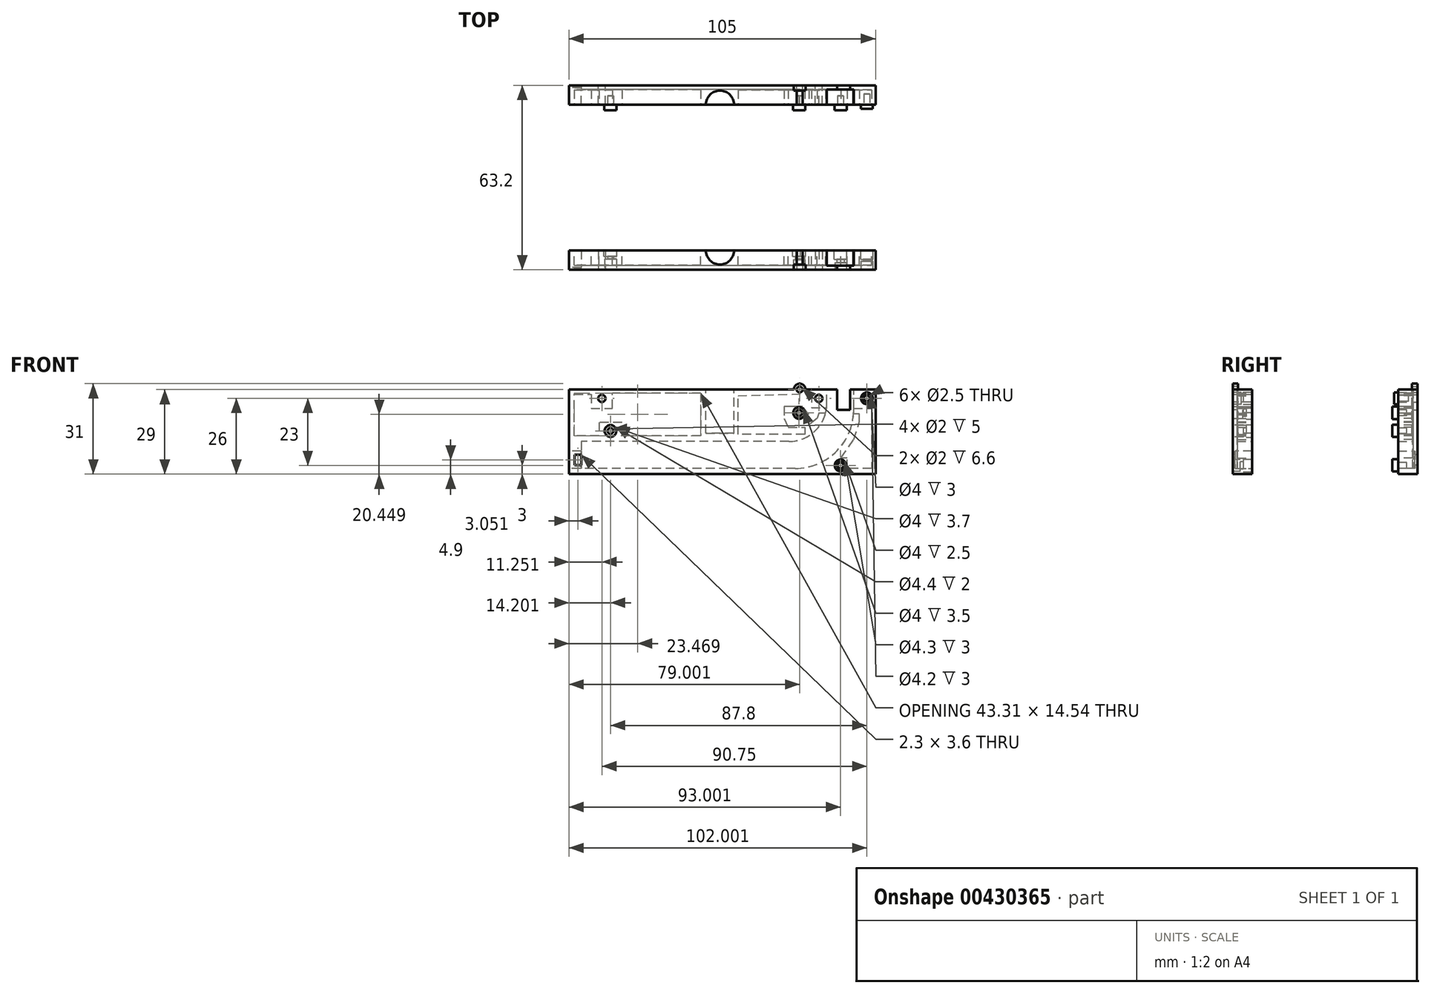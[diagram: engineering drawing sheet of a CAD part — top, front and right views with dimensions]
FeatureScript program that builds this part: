
annotation { "Feature Type Name" : "Feature", "Feature Type Description" : "" }
export const myFeature = defineFeature(function(context is Context, id is Id, definition is map)
    precondition{}
    {
        {
            var Q0;
            Q0=qCreatedBy(makeId("Front.planeOp"),FACE);
            var sketch = newSketch(context, id + "F0", { "sketchPlane" : qUnion([Q0])});
            skLineSegment(sketch, "E0.bottom", {"start": v(-55.53, -4.5) * mm, "end": v(49.47, -4.5) * mm});
            skLineSegment(sketch, "E0.top", {"start": v(-55.53, -33.5) * mm, "end": v(49.47, -33.5) * mm});
            skLineSegment(sketch, "E0.left", {"start": v(-55.53, -4.5) * mm, "end": v(-55.53, -33.5) * mm});
            skLineSegment(sketch, "E0.right", {"start": v(49.47, -4.5) * mm, "end": v(49.47, -33.5) * mm});
            skSolve(sketch);
        }
        {
            var Q0;
            Q0 = qSketchRegion(id + "F0", true);
            extrude(context, id + "F1", {"entities" : qUnion([Q0]), "depth" : 6.6 * mm});
        }
        {
            var Q0;
            Q0=makeQuery(id+"F1.opExtrude","CAP_FACE",FACE,{"disambiguationData":[OSD([sQuery(id+"F0.wireOp",EDGE,"E0.bottom"),sQuery(id+"F0.wireOp",EDGE,"E0.top"),sQuery(id+"F0.wireOp",EDGE,"E0.left"),sQuery(id+"F0.wireOp",EDGE,"E0.right")])],"isStart":false});
            var sketch = newSketch(context, id + "F2", { "sketchPlane" : qUnion([Q0])});
            skCircle(sketch, "E1", {"center": v(46.47, -7.5) * mm, "radius": 2 * mm});
            skSolve(sketch);
        }
        {
            var Q0;
            Q0 = qSketchRegion(id + "F2", true);
            extrude(context, id + "F3", {"entities" : qUnion([Q0]), "operationType" : NewBodyOperationType.REMOVE, "oppositeDirection" : true, "depth" : 3 * mm});
        }
        {
            var Q0;
            Q0=makeQuery(id+"F3.boolean.opBoolean","COPY",FACE,{"derivedFrom":makeQuery(id+"F3.opExtrude","CAP_FACE",FACE,{"disambiguationData":[OSD([sQuery(id+"F2.wireOp",EDGE,"E1")])],"isStart":false})});
            var sketch = newSketch(context, id + "F4", { "sketchPlane" : qUnion([Q0])});
            skCircle(sketch, "E2", {"center": v(46.47, -7.5) * mm, "radius": 1.25 * mm});
            skSolve(sketch);
        }
        {
            var Q0;
            Q0 = qSketchRegion(id + "F4", true);
            extrude(context, id + "F5", {"entities" : qUnion([Q0]), "operationType" : NewBodyOperationType.REMOVE, "oppositeDirection" : true, "depth" : 25 * mm});
        }
        {
            var Q0;
            Q0=makeQuery(id+"F1.opExtrude","CAP_FACE",FACE,{"disambiguationData":[OSD([sQuery(id+"F0.wireOp",EDGE,"E0.bottom"),sQuery(id+"F0.wireOp",EDGE,"E0.top"),sQuery(id+"F0.wireOp",EDGE,"E0.left"),sQuery(id+"F0.wireOp",EDGE,"E0.right")])],"isStart":false});
            var sketch = newSketch(context, id + "F6", { "sketchPlane" : qUnion([Q0])});
            skCircle(sketch, "E3", {"center": v(30.02, -7.55) * mm, "radius": 1.25 * mm});
            skSolve(sketch);
        }
        {
            var Q0;
            Q0 = qSketchRegion(id + "F6", true);
            extrude(context, id + "F7", {"entities" : qUnion([Q0]), "operationType" : NewBodyOperationType.REMOVE, "oppositeDirection" : true, "depth" : 25 * mm});
        }
        {
            var Q0;
            Q0=makeQuery(id+"F1.opExtrude","CAP_FACE",FACE,{"disambiguationData":[OSD([sQuery(id+"F0.wireOp",EDGE,"E0.bottom"),sQuery(id+"F0.wireOp",EDGE,"E0.top"),sQuery(id+"F0.wireOp",EDGE,"E0.left"),sQuery(id+"F0.wireOp",EDGE,"E0.right")])],"isStart":false});
            var sketch = newSketch(context, id + "F8", { "sketchPlane" : qUnion([Q0])});
            skCircle(sketch, "E4", {"center": v(23.27, -12.5) * mm, "radius": 1 * mm});
            skSolve(sketch);
        }
        {
            var Q0;
            Q0 = qSketchRegion(id + "F8", true);
            extrude(context, id + "F9", {"entities" : qUnion([Q0]), "operationType" : NewBodyOperationType.REMOVE, "oppositeDirection" : true, "depth" : 3.7 * mm});
        }
        {
            var Q0;
            Q0=makeQuery(id+"F9.boolean.opBoolean","COPY",FACE,{"derivedFrom":makeQuery(id+"F9.opExtrude","CAP_FACE",FACE,{"disambiguationData":[OSD([sQuery(id+"F8.wireOp",EDGE,"E4")])],"isStart":false})});
            var sketch = newSketch(context, id + "F10", { "sketchPlane" : qUnion([Q0])});
            skCircle(sketch, "E5", {"center": v(23.27, -12.5) * mm, "radius": 1.3 * mm});
            skSolve(sketch);
        }
        {
            var Q0;
            Q0 = qSketchRegion(id + "F10", true);
            extrude(context, id + "F11", {"entities" : qUnion([Q0]), "operationType" : NewBodyOperationType.REMOVE, "oppositeDirection" : true, "depth" : 25 * mm});
        }
        {
            var Q0;
            Q0=makeQuery(id+"F1.opExtrude","CAP_FACE",FACE,{"disambiguationData":[OSD([sQuery(id+"F0.wireOp",EDGE,"E0.bottom"),sQuery(id+"F0.wireOp",EDGE,"E0.top"),sQuery(id+"F0.wireOp",EDGE,"E0.left"),sQuery(id+"F0.wireOp",EDGE,"E0.right")])],"isStart":false});
            var sketch = newSketch(context, id + "F12", { "sketchPlane" : qUnion([Q0])});
            skCircle(sketch, "E6", {"center": v(-44.28, -7.55) * mm, "radius": 1.25 * mm});
            skSolve(sketch);
        }
        {
            var Q0;
            Q0 = qSketchRegion(id + "F12", true);
            extrude(context, id + "F13", {"entities" : qUnion([Q0]), "operationType" : NewBodyOperationType.REMOVE, "oppositeDirection" : true, "depth" : 25 * mm});
        }
        {
            var Q0;
            Q0=makeQuery(id+"F1.opExtrude","CAP_FACE",FACE,{"disambiguationData":[OSD([sQuery(id+"F0.wireOp",EDGE,"E0.bottom"),sQuery(id+"F0.wireOp",EDGE,"E0.top"),sQuery(id+"F0.wireOp",EDGE,"E0.left"),sQuery(id+"F0.wireOp",EDGE,"E0.right")])],"isStart":false});
            var sketch = newSketch(context, id + "F14", { "sketchPlane" : qUnion([Q0])});
            skCircle(sketch, "E7", {"center": v(-41.33, -18.7) * mm, "radius": 2 * mm});
            skSolve(sketch);
        }
        {
            var Q0;
            Q0 = qSketchRegion(id + "F14", true);
            extrude(context, id + "F15", {"entities" : qUnion([Q0]), "operationType" : NewBodyOperationType.REMOVE, "oppositeDirection" : true, "depth" : 3.7 * mm});
        }
        {
            var Q0;
            Q0=makeQuery(id+"F15.boolean.opBoolean","COPY",FACE,{"derivedFrom":makeQuery(id+"F15.opExtrude","CAP_FACE",FACE,{"disambiguationData":[OSD([sQuery(id+"F14.wireOp",EDGE,"E7")])],"isStart":false})});
            var sketch = newSketch(context, id + "F16", { "sketchPlane" : qUnion([Q0])});
            skCircle(sketch, "E8", {"center": v(-41.33, -18.7) * mm, "radius": 1 * mm});
            skSolve(sketch);
        }
        {
            var Q0;
            Q0 = qSketchRegion(id + "F16", true);
            extrude(context, id + "F17", {"entities" : qUnion([Q0]), "operationType" : NewBodyOperationType.REMOVE, "oppositeDirection" : true, "depth" : 25 * mm});
        }
        {
            var Q0;
            Q0=makeQuery(id+"F1.opExtrude","CAP_FACE",FACE,{"disambiguationData":[OSD([sQuery(id+"F0.wireOp",EDGE,"E0.bottom"),sQuery(id+"F0.wireOp",EDGE,"E0.top"),sQuery(id+"F0.wireOp",EDGE,"E0.left"),sQuery(id+"F0.wireOp",EDGE,"E0.right")])],"isStart":false});
            var sketch = newSketch(context, id + "F18", { "sketchPlane" : qUnion([Q0])});
            skCircle(sketch, "E9", {"center": v(37.47, -30.5) * mm, "radius": 2 * mm});
            skSolve(sketch);
        }
        {
            var Q0;
            Q0 = qSketchRegion(id + "F18", true);
            extrude(context, id + "F19", {"entities" : qUnion([Q0]), "operationType" : NewBodyOperationType.REMOVE, "oppositeDirection" : true, "depth" : 2.5 * mm});
        }
        {
            var Q0;
            Q0=makeQuery(id+"F19.boolean.opBoolean","COPY",FACE,{"derivedFrom":makeQuery(id+"F19.opExtrude","CAP_FACE",FACE,{"disambiguationData":[OSD([sQuery(id+"F18.wireOp",EDGE,"E9")])],"isStart":false})});
            var sketch = newSketch(context, id + "F20", { "sketchPlane" : qUnion([Q0])});
            skCircle(sketch, "E10", {"center": v(37.47, -30.5) * mm, "radius": 1.25 * mm});
            skSolve(sketch);
        }
        {
            var Q0;
            Q0 = qSketchRegion(id + "F20", true);
            extrude(context, id + "F21", {"entities" : qUnion([Q0]), "operationType" : NewBodyOperationType.REMOVE, "oppositeDirection" : true, "depth" : 25 * mm});
        }
        {
            var Q0;
            Q0=makeQuery(id+"F1.opExtrude","CAP_FACE",FACE,{"disambiguationData":[OSD([sQuery(id+"F0.wireOp",EDGE,"E0.bottom"),sQuery(id+"F0.wireOp",EDGE,"E0.top"),sQuery(id+"F0.wireOp",EDGE,"E0.left"),sQuery(id+"F0.wireOp",EDGE,"E0.right")])],"isStart":false});
            var sketch = newSketch(context, id + "F22", { "sketchPlane" : qUnion([Q0])});
            skLineSegment(sketch, "E11.bottom", {"start": v(36.27, -4.5) * mm, "end": v(40.77, -4.5) * mm});
            skLineSegment(sketch, "E11.top", {"start": v(36.27, -11.5) * mm, "end": v(40.77, -11.5) * mm});
            skLineSegment(sketch, "E11.left", {"start": v(36.27, -4.5) * mm, "end": v(36.27, -11.5) * mm});
            skLineSegment(sketch, "E11.right", {"start": v(40.77, -4.5) * mm, "end": v(40.77, -11.5) * mm});
            skSolve(sketch);
        }
        {
            var Q0;
            Q0 = qSketchRegion(id + "F22", true);
            extrude(context, id + "F23", {"entities" : qUnion([Q0]), "operationType" : NewBodyOperationType.REMOVE, "oppositeDirection" : true, "depth" : 25 * mm});
        }
        {
            var Q0;
            Q0=makeQuery(id+"F1.opExtrude","CAP_FACE",FACE,{"disambiguationData":[OSD([sQuery(id+"F0.wireOp",EDGE,"E0.bottom"),sQuery(id+"F0.wireOp",EDGE,"E0.top"),sQuery(id+"F0.wireOp",EDGE,"E0.left"),sQuery(id+"F0.wireOp",EDGE,"E0.right")])],"isStart":false});
            var sketch = newSketch(context, id + "F24", { "sketchPlane" : qUnion([Q0])});
            skCircle(sketch, "E12", {"center": v(23.47, -4.5) * mm, "radius": 2 * mm});
            skSolve(sketch);
        }
        {
            var Q0;
            Q0 = qSketchRegion(id + "F24", true);
            extrude(context, id + "F25", {"entities" : qUnion([Q0]), "operationType" : NewBodyOperationType.ADD, "oppositeDirection" : true, "depth" : 1.8 * mm});
        }
        {
            var Q0;
            Q0=makeQuery(id+"F25.boolean.opBoolean","MERGE",FACE,{"derivedFrom":[makeQuery(id+"F1.opExtrude","CAP_FACE",FACE,{"disambiguationData":[OSD([sQuery(id+"F0.wireOp",EDGE,"E0.bottom"),sQuery(id+"F0.wireOp",EDGE,"E0.top"),sQuery(id+"F0.wireOp",EDGE,"E0.left"),sQuery(id+"F0.wireOp",EDGE,"E0.right")])],"isStart":false}),makeQuery(id+"F25.opExtrude","CAP_FACE",FACE,{"disambiguationData":[OSD([sQuery(id+"F24.wireOp",EDGE,"E12")])],"isStart":true})]});
            var sketch = newSketch(context, id + "F26", { "sketchPlane" : qUnion([Q0])});
            skCircle(sketch, "E13", {"center": v(23.47, -4.5) * mm, "radius": 1 * mm});
            skSolve(sketch);
        }
        {
            var Q0;
            Q0 = qSketchRegion(id + "F26", true);
            extrude(context, id + "F27", {"entities" : qUnion([Q0]), "operationType" : NewBodyOperationType.REMOVE, "oppositeDirection" : true, "depth" : 25 * mm});
        }
        {
            var Q0;
            Q0=makeQuery(id+"F25.boolean.opBoolean","MERGE",FACE,{"derivedFrom":[makeQuery(id+"F1.opExtrude","CAP_FACE",FACE,{"disambiguationData":[OSD([sQuery(id+"F0.wireOp",EDGE,"E0.bottom"),sQuery(id+"F0.wireOp",EDGE,"E0.top"),sQuery(id+"F0.wireOp",EDGE,"E0.left"),sQuery(id+"F0.wireOp",EDGE,"E0.right")])],"isStart":false}),makeQuery(id+"F25.opExtrude","CAP_FACE",FACE,{"disambiguationData":[OSD([sQuery(id+"F24.wireOp",EDGE,"E12")])],"isStart":true})]});
            var sketch = newSketch(context, id + "F28", { "sketchPlane" : qUnion([Q0])});
            skLineSegment(sketch, "E14.bottom", {"start": v(-42.43, -33.5) * mm, "end": v(35.07, -33.5) * mm});
            skLineSegment(sketch, "E14.top", {"start": v(-42.43, -32.1) * mm, "end": v(35.07, -32.1) * mm});
            skLineSegment(sketch, "E14.left", {"start": v(-42.43, -33.5) * mm, "end": v(-42.43, -32.1) * mm});
            skLineSegment(sketch, "E14.right", {"start": v(35.07, -33.5) * mm, "end": v(35.07, -32.1) * mm});
            skSolve(sketch);
        }
        {
            var Q0;
            Q0=makeQuery(id+"F1.opExtrude","CAP_FACE",FACE,{"disambiguationData":[OSD([sQuery(id+"F0.wireOp",EDGE,"E0.bottom"),sQuery(id+"F0.wireOp",EDGE,"E0.top"),sQuery(id+"F0.wireOp",EDGE,"E0.left"),sQuery(id+"F0.wireOp",EDGE,"E0.right")])],"isStart":true});
            var sketch = newSketch(context, id + "F29", { "sketchPlane" : qUnion([Q0])});
            skArc(sketch, "E15", {"start": v(-41.96, -10.9) * mm, "mid": v(-36.32, -25.43) * mm, "end": v(-21.97, -31.5) * mm});
            skLineSegment(sketch, "E16", {"start": v(-41.96, -12.1) * mm, "end": v(-41.96, -4.5) * mm});
            skLineSegment(sketch, "E17", {"start": v(-41.96, -4.5) * mm, "end": v(-40.77, -4.5) * mm});
            skLineSegment(sketch, "E18", {"start": v(-21.97, -31.5) * mm, "end": v(55.53, -31.5) * mm});
            skLineSegment(sketch, "E19", {"start": v(-40.77, -4.5) * mm, "end": v(-40.77, -11.5) * mm});
            skLineSegment(sketch, "E20", {"start": v(-40.77, -11.5) * mm, "end": v(-36.27, -11.5) * mm});
            skLineSegment(sketch, "E21", {"start": v(-36.27, -11.5) * mm, "end": v(-36.27, -4.5) * mm});
            skLineSegment(sketch, "E22", {"start": v(-36.27, -4.5) * mm, "end": v(-32.76, -4.5) * mm});
            skArc(sketch, "E23", {"start": v(-32.76, -9.3) * mm, "mid": v(-28.95, -18.5) * mm, "end": v(-19.76, -22.3) * mm});
            skLineSegment(sketch, "E24", {"start": v(-32.76, -9.3) * mm, "end": v(-32.76, -4.5) * mm});
            skLineSegment(sketch, "E25", {"start": v(-19.76, -22.3) * mm, "end": v(-17.97, -22.3) * mm});
            skLineSegment(sketch, "E26", {"start": v(-17.97, -22.3) * mm, "end": v(55.53, -22.3) * mm});
            skLineSegment(sketch, "E27", {"start": v(55.53, -31.5) * mm, "end": v(55.53, -22.3) * mm});
            skSolve(sketch);
        }
        {
            var Q0;
            Q0 = qSketchRegion(id + "F29", true);
            extrude(context, id + "F30", {"entities" : qUnion([Q0]), "operationType" : NewBodyOperationType.REMOVE, "oppositeDirection" : true, "depth" : 5.1 * mm});
        }
        {
            var Q0;
            Q0=makeQuery(id+"F30.boolean.opBoolean","COPY",FACE,{"derivedFrom":makeQuery(id+"F30.opExtrude","CAP_FACE",FACE,{"disambiguationData":[OSD([sQuery(id+"F29.wireOp",EDGE,"E15"),sQuery(id+"F29.wireOp",EDGE,"E16"),sQuery(id+"F29.wireOp",EDGE,"E17"),sQuery(id+"F29.wireOp",EDGE,"E18"),sQuery(id+"F29.wireOp",EDGE,"E19"),sQuery(id+"F29.wireOp",EDGE,"E20"),sQuery(id+"F29.wireOp",EDGE,"E21"),sQuery(id+"F29.wireOp",EDGE,"E22"),sQuery(id+"F29.wireOp",EDGE,"E23"),sQuery(id+"F29.wireOp",EDGE,"E24"),sQuery(id+"F29.wireOp",EDGE,"E25"),sQuery(id+"F29.wireOp",EDGE,"E26"),sQuery(id+"F29.wireOp",EDGE,"E27")])],"isStart":false})});
            var sketch = newSketch(context, id + "F31", { "sketchPlane" : qUnion([Q0])});
            skLineSegment(sketch, "E28.bottom", {"start": v(51.33, -26.8) * mm, "end": v(53.63, -26.8) * mm});
            skLineSegment(sketch, "E28.top", {"start": v(51.33, -30.4) * mm, "end": v(53.63, -30.4) * mm});
            skLineSegment(sketch, "E28.left", {"start": v(51.33, -26.8) * mm, "end": v(51.33, -30.4) * mm});
            skLineSegment(sketch, "E28.right", {"start": v(53.63, -26.8) * mm, "end": v(53.63, -30.4) * mm});
            skSolve(sketch);
        }
        {
            var Q0;
            Q0 = qSketchRegion(id + "F31", true);
            extrude(context, id + "F32", {"entities" : qUnion([Q0]), "operationType" : NewBodyOperationType.REMOVE, "oppositeDirection" : true, "depth" : 25 * mm});
        }
        {
            var Q0;
            {var subQ0=sQuery(id+"F0.wireOp",EDGE,"E0.left");var subQ1=makeQuery(id+"F1.opExtrude","SWEPT_FACE",FACE,{"disambiguationData":[OSD([subQ0])]});var subQ5=sQuery(id+"F0.wireOp",EDGE,"E0.bottom");Q0=makeQuery(id+"F27.boolean.opBoolean","SPLIT",FACE,{"disambiguationData":[TD([subQ1])],"derivedFrom":makeQuery(id+"F23.boolean.opBoolean","SPLIT",FACE,{"disambiguationData":[TD([subQ1])],"derivedFrom":makeQuery(id+"F1.opExtrude","SWEPT_FACE",FACE,{"disambiguationData":[OSD([subQ5])]})})});}
            var sketch = newSketch(context, id + "F33", { "sketchPlane" : qUnion([Q0])});
            skCircle(sketch, "E29", {"center": v(-3.83, 0) * mm, "radius": 4.8 * mm});
            skSolve(sketch);
        }
        {
            var Q0;
            Q0 = qSketchRegion(id + "F33", true);
            extrude(context, id + "F34", {"entities" : qUnion([Q0]), "operationType" : NewBodyOperationType.REMOVE, "oppositeDirection" : true, "depth" : 15 * mm});
        }
        {
            var Q0;
            {var subQ0=sQuery(id+"F0.wireOp",EDGE,"E0.left");var subQ1=sQuery(id+"F0.wireOp",EDGE,"E0.top");var subQ2=sQuery(id+"F0.wireOp",EDGE,"E0.right");var subQ3=sQuery(id+"F0.wireOp",EDGE,"E0.bottom");Q0=makeQuery(id+"F30.boolean.opBoolean","SPLIT",FACE,{"disambiguationData":[TD([makeQuery(id+"F1.opExtrude","SWEPT_FACE",FACE,{"disambiguationData":[OSD([subQ1])]})])],"derivedFrom":makeQuery(id+"F1.opExtrude","CAP_FACE",FACE,{"disambiguationData":[OSD([subQ3,subQ1,subQ0,subQ2])],"isStart":true})});}
            var sketch = newSketch(context, id + "F35", { "sketchPlane" : qUnion([Q0])});
            skLineSegment(sketch, "E30", {"start": v(-48.12, -10.9) * mm, "end": v(-48.12, -31.52) * mm});
            skLineSegment(sketch, "E31", {"start": v(-48.12, -31.52) * mm, "end": v(-39.74, -31.52) * mm});
            skLineSegment(sketch, "E32", {"start": v(-39.74, -31.52) * mm, "end": v(-39.74, -27.95) * mm});
            skLineSegment(sketch, "E33", {"start": v(-39.74, -27.95) * mm, "end": v(-37.62, -27.95) * mm});
            skLineSegment(sketch, "E34", {"start": v(-37.62, -27.95) * mm, "end": v(-41.96, -21.67) * mm});
            skLineSegment(sketch, "E35", {"start": v(-41.96, -21.67) * mm, "end": v(-43.9, -15.56) * mm});
            skLineSegment(sketch, "E36", {"start": v(-43.9, -15.56) * mm, "end": v(-43.9, -10.9) * mm});
            skLineSegment(sketch, "E37", {"start": v(-43.9, -10.9) * mm, "end": v(-48.12, -10.9) * mm});
            skSolve(sketch);
        }
        {
            var Q0;
            Q0 = qSketchRegion(id + "F35", true);
            extrude(context, id + "F36", {"entities" : qUnion([Q0]), "operationType" : NewBodyOperationType.REMOVE, "oppositeDirection" : true, "depth" : 5 * mm});
        }
        {
            var Q0;
            {var subQ0=sQuery(id+"F0.wireOp",EDGE,"E0.left");var subQ1=sQuery(id+"F0.wireOp",EDGE,"E0.bottom");Q0=makeQuery(id+"F30.boolean.opBoolean","SPLIT",FACE,{"disambiguationData":[TD([makeQuery(id+"F7.boolean.opBoolean","COPY",FACE,{"derivedFrom":makeQuery(id+"F7.opExtrude","SWEPT_FACE",FACE,{"disambiguationData":[OSD([sQuery(id+"F6.wireOp",EDGE,"E3")])]})})])],"derivedFrom":makeQuery(id+"F1.opExtrude","CAP_FACE",FACE,{"disambiguationData":[OSD([subQ1,sQuery(id+"F0.wireOp",EDGE,"E0.top"),subQ0,sQuery(id+"F0.wireOp",EDGE,"E0.right")])],"isStart":true})});}
            var sketch = newSketch(context, id + "F37", { "sketchPlane" : qUnion([Q0])});
            skLineSegment(sketch, "E38", {"start": v(-27.5, -5.96) * mm, "end": v(-27.5, -10.66) * mm});
            skLineSegment(sketch, "E39", {"start": v(-27.5, -10.66) * mm, "end": v(-30.68, -10.66) * mm});
            skLineSegment(sketch, "E40", {"start": v(-30.68, -10.66) * mm, "end": v(-29.4, -14.42) * mm});
            skLineSegment(sketch, "E41", {"start": v(-29.4, -14.42) * mm, "end": v(-26.6, -16.64) * mm});
            skLineSegment(sketch, "E42", {"start": v(-26.6, -16.64) * mm, "end": v(-26.6, -13.1) * mm});
            skLineSegment(sketch, "E43", {"start": v(-26.6, -13.1) * mm, "end": v(-24.44, -10.35) * mm});
            skLineSegment(sketch, "E44", {"start": v(-24.44, -10.35) * mm, "end": v(-20.5, -10.35) * mm});
            skLineSegment(sketch, "E45", {"start": v(-20.5, -10.35) * mm, "end": v(-18.12, -10.35) * mm});
            skLineSegment(sketch, "E46", {"start": v(-18.12, -10.35) * mm, "end": v(-18.12, -14.42) * mm});
            skLineSegment(sketch, "E47", {"start": v(-18.12, -14.42) * mm, "end": v(-19.56, -17.41) * mm});
            skLineSegment(sketch, "E48", {"start": v(-19.56, -17.41) * mm, "end": v(-22.65, -17.41) * mm});
            skLineSegment(sketch, "E49", {"start": v(-22.65, -17.41) * mm, "end": v(-25.24, -17.41) * mm});
            skPoint(sketch, "E49.endSnap0", {"position": v(-21.1, -17.41) * mm});
            skLineSegment(sketch, "E50", {"start": v(-25.24, -17.41) * mm, "end": v(-25.24, -19.84) * mm});
            skLineSegment(sketch, "E51", {"start": v(-25.24, -19.84) * mm, "end": v(-2.35, -19.84) * mm});
            skLineSegment(sketch, "E52", {"start": v(-2.35, -19.84) * mm, "end": v(-2.35, -6.6) * mm});
            skLineSegment(sketch, "E53", {"start": v(-2.35, -6.6) * mm, "end": v(-27.5, -5.96) * mm});
            skSolve(sketch);
        }
        {
            var Q0;
            Q0 = qSketchRegion(id + "F37", true);
            extrude(context, id + "F38", {"entities" : qUnion([Q0]), "operationType" : NewBodyOperationType.REMOVE, "oppositeDirection" : true, "depth" : 5 * mm});
        }
        {
            var Q0;
            {var subQ0=sQuery(id+"F0.wireOp",EDGE,"E0.left");var subQ1=sQuery(id+"F0.wireOp",EDGE,"E0.bottom");Q0=makeQuery(id+"F30.boolean.opBoolean","SPLIT",FACE,{"disambiguationData":[TD([makeQuery(id+"F7.boolean.opBoolean","COPY",FACE,{"derivedFrom":makeQuery(id+"F7.opExtrude","SWEPT_FACE",FACE,{"disambiguationData":[OSD([sQuery(id+"F6.wireOp",EDGE,"E3")])]})})])],"derivedFrom":makeQuery(id+"F1.opExtrude","CAP_FACE",FACE,{"disambiguationData":[OSD([subQ1,sQuery(id+"F0.wireOp",EDGE,"E0.top"),subQ0,sQuery(id+"F0.wireOp",EDGE,"E0.right")])],"isStart":true})});}
            var sketch = newSketch(context, id + "F39", { "sketchPlane" : qUnion([Q0])});
            skLineSegment(sketch, "E54", {"start": v(10.4, -5.78) * mm, "end": v(10.4, -20.32) * mm});
            skLineSegment(sketch, "E55", {"start": v(10.4, -20.32) * mm, "end": v(37.36, -20.32) * mm});
            skLineSegment(sketch, "E56", {"start": v(37.36, -20.32) * mm, "end": v(37.36, -15.78) * mm});
            skLineSegment(sketch, "E57", {"start": v(37.36, -15.78) * mm, "end": v(45.24, -15.78) * mm});
            skLineSegment(sketch, "E58", {"start": v(45.24, -15.78) * mm, "end": v(45.24, -20.32) * mm});
            skLineSegment(sketch, "E59", {"start": v(45.24, -20.32) * mm, "end": v(53.72, -20.32) * mm});
            skLineSegment(sketch, "E60", {"start": v(53.72, -20.32) * mm, "end": v(53.72, -6.19) * mm});
            skLineSegment(sketch, "E61", {"start": v(53.72, -6.19) * mm, "end": v(47.96, -6.19) * mm});
            skLineSegment(sketch, "E62", {"start": v(47.96, -6.19) * mm, "end": v(47.96, -10.93) * mm});
            skLineSegment(sketch, "E63", {"start": v(47.96, -10.93) * mm, "end": v(40.7, -10.93) * mm});
            skLineSegment(sketch, "E64", {"start": v(40.7, -10.93) * mm, "end": v(40.7, -6.19) * mm});
            skLineSegment(sketch, "E65", {"start": v(10.4, -5.78) * mm, "end": v(40.7, -5.78) * mm});
            skLineSegment(sketch, "E66", {"start": v(40.7, -5.78) * mm, "end": v(40.7, -6.19) * mm});
            skSolve(sketch);
        }
        {
            var Q0;
            Q0 = qSketchRegion(id + "F39", true);
            extrude(context, id + "F40", {"entities" : qUnion([Q0]), "operationType" : NewBodyOperationType.REMOVE, "oppositeDirection" : true, "depth" : 5 * mm});
        }
        {
            var Q0;
            Q0=qCreatedBy(makeId("Front.planeOp"),FACE);
            cPlane(context, id + "F41", {"entities" : qUnion([Q0]), "cplaneType" : CPlaneType.OFFSET, "offset" : 25 * mm, "oppositeDirection" : true, "width" : 150 * mm, "height" : 150 * mm});
        }
        {
            var Q0;
            {var subQ0=sQuery(id+"F0.wireOp",EDGE,"E0.left");var subQ1=sQuery(id+"F0.wireOp",EDGE,"E0.top");var subQ2=sQuery(id+"F0.wireOp",EDGE,"E0.right");var subQ3=sQuery(id+"F0.wireOp",EDGE,"E0.bottom");Q0=makeQuery(id+"F30.boolean.opBoolean","SPLIT",FACE,{"disambiguationData":[TD([makeQuery(id+"F1.opExtrude","SWEPT_FACE",FACE,{"disambiguationData":[OSD([subQ1])]})])],"derivedFrom":makeQuery(id+"F1.opExtrude","CAP_FACE",FACE,{"disambiguationData":[OSD([subQ3,subQ1,subQ0,subQ2])],"isStart":true})});}
            var sketch = newSketch(context, id + "F42", { "sketchPlane" : qUnion([Q0])});
            skLineSegment(sketch, "E67.bottom", {"start": v(-43.9, -10.9) * mm, "end": v(-41.75, -10.9) * mm});
            skLineSegment(sketch, "E67.top", {"start": v(-43.9, -12.9) * mm, "end": v(-41.75, -12.9) * mm});
            skLineSegment(sketch, "E67.left", {"start": v(-43.9, -10.9) * mm, "end": v(-43.9, -12.9) * mm});
            skLineSegment(sketch, "E67.right", {"start": v(-41.75, -10.9) * mm, "end": v(-41.75, -12.9) * mm});
            skSolve(sketch);
        }
        {
            var Q0;
            Q0 = qSketchRegion(id + "F42", true);
            extrude(context, id + "F43", {"entities" : qUnion([Q0]), "operationType" : NewBodyOperationType.REMOVE, "oppositeDirection" : true, "depth" : 5 * mm});
        }
        {
            var Q0;
            {var subQ0=sQuery(id+"F0.wireOp",EDGE,"E0.left");var subQ1=sQuery(id+"F0.wireOp",EDGE,"E0.bottom");Q0=makeQuery(id+"F30.boolean.opBoolean","SPLIT",FACE,{"disambiguationData":[TD([makeQuery(id+"F7.boolean.opBoolean","COPY",FACE,{"derivedFrom":makeQuery(id+"F7.opExtrude","SWEPT_FACE",FACE,{"disambiguationData":[OSD([sQuery(id+"F6.wireOp",EDGE,"E3")])]})})])],"derivedFrom":makeQuery(id+"F1.opExtrude","CAP_FACE",FACE,{"disambiguationData":[OSD([subQ1,sQuery(id+"F0.wireOp",EDGE,"E0.top"),subQ0,sQuery(id+"F0.wireOp",EDGE,"E0.right")])],"isStart":true})});}
            var sketch = newSketch(context, id + "F44", { "sketchPlane" : qUnion([Q0])});
            skPoint(sketch, "E68.oppositeSnap0", {"position": v(-30.04, -12.54) * mm});
            skLineSegment(sketch, "E68.bottom", {"start": v(-33.85, -10.66) * mm, "end": v(-30.04, -10.66) * mm});
            skLineSegment(sketch, "E68.top", {"start": v(-33.85, -12.66) * mm, "end": v(-30.04, -12.66) * mm});
            skLineSegment(sketch, "E68.left", {"start": v(-33.85, -10.66) * mm, "end": v(-33.85, -12.66) * mm});
            skLineSegment(sketch, "E68.right", {"start": v(-30.04, -10.66) * mm, "end": v(-30.04, -12.66) * mm});
            skSolve(sketch);
        }
        {
            var Q0;
            Q0 = qSketchRegion(id + "F44", true);
            extrude(context, id + "F45", {"entities" : qUnion([Q0]), "operationType" : NewBodyOperationType.REMOVE, "oppositeDirection" : true, "depth" : 5 * mm});
        }
        {
            var Q0;
            Q0=makeQuery(id+"F30.boolean.opBoolean","COPY",FACE,{"derivedFrom":makeQuery(id+"F30.opExtrude","CAP_FACE",FACE,{"disambiguationData":[OSD([sQuery(id+"F29.wireOp",EDGE,"E15"),sQuery(id+"F29.wireOp",EDGE,"E16"),sQuery(id+"F29.wireOp",EDGE,"E17"),sQuery(id+"F29.wireOp",EDGE,"E18"),sQuery(id+"F29.wireOp",EDGE,"E19"),sQuery(id+"F29.wireOp",EDGE,"E20"),sQuery(id+"F29.wireOp",EDGE,"E21"),sQuery(id+"F29.wireOp",EDGE,"E22"),sQuery(id+"F29.wireOp",EDGE,"E23"),sQuery(id+"F29.wireOp",EDGE,"E24"),sQuery(id+"F29.wireOp",EDGE,"E25"),sQuery(id+"F29.wireOp",EDGE,"E26"),sQuery(id+"F29.wireOp",EDGE,"E27")])],"isStart":false})});
            var sketch = newSketch(context, id + "F46", { "sketchPlane" : qUnion([Q0])});
            skLineSegment(sketch, "E69.bottom", {"start": v(51.33, -31.5) * mm, "end": v(55.53, -31.5) * mm});
            skLineSegment(sketch, "E69.top", {"start": v(51.33, -22.3) * mm, "end": v(55.53, -22.3) * mm});
            skLineSegment(sketch, "E69.left", {"start": v(51.33, -31.5) * mm, "end": v(51.33, -22.3) * mm});
            skLineSegment(sketch, "E69.right", {"start": v(55.53, -31.5) * mm, "end": v(55.53, -22.3) * mm});
            skSolve(sketch);
        }
        {
            var Q0;
            Q0 = qSketchRegion(id + "F46", true);
            extrude(context, id + "F47", {"entities" : qUnion([Q0]), "operationType" : NewBodyOperationType.REMOVE, "oppositeDirection" : true, "depth" : 0.7 * mm});
        }
        {
            var Q0;
            Q0=makeQuery(id+"F1.opExtrude","SWEPT_BODY",BODY,{"disambiguationData":[OSD([sQuery(id+"F0.wireOp",EDGE,"E0.bottom"),sQuery(id+"F0.wireOp",EDGE,"E0.top"),sQuery(id+"F0.wireOp",EDGE,"E0.left"),sQuery(id+"F0.wireOp",EDGE,"E0.right")])]});
            var Q1;
            Q1=qCreatedBy(id+"F41.planeOp",FACE);
            mirror(context, id + "F48", {"entities" : qUnion([Q0]), "mirrorPlane" : qUnion([Q1])});
        }
        {
            var Q0;
            Q0=makeQuery(id+"F48.opPattern","COPY",FACE,{"derivedFrom":makeQuery(id+"F3.boolean.opBoolean","COPY",FACE,{"derivedFrom":makeQuery(id+"F3.opExtrude","CAP_FACE",FACE,{"disambiguationData":[OSD([sQuery(id+"F2.wireOp",EDGE,"E1")])],"isStart":false})}),"instanceName":"1"});
            var sketch = newSketch(context, id + "F49", { "sketchPlane" : qUnion([Q0])});
            skCircle(sketch, "E70", {"center": v(-46.47, -7.5) * mm, "radius": 2.02 * mm});
            skSolve(sketch);
        }
        {
            var Q0;
            Q0 = qSketchRegion(id + "F49", true);
            extrude(context, id + "F50", {"entities" : qUnion([Q0]), "operationType" : NewBodyOperationType.ADD, "oppositeDirection" : true, "depth" : 5 * mm, "hasSecondDirection" : true, "secondDirectionOppositeDirection" : false, "secondDirectionDepth" : 3 * mm});
        }
        {
            var Q0;
            Q0=makeQuery(id+"F50.opExtrude","CAP_FACE",FACE,{"disambiguationData":[OSD([sQuery(id+"F49.wireOp",EDGE,"E70")])],"isStart":false});
            var sketch = newSketch(context, id + "F51", { "sketchPlane" : qUnion([Q0])});
            skCircle(sketch, "E71", {"center": v(46.47, -7.5) * mm, "radius": 1.95 * mm});
            skCircle(sketch, "E72", {"center": v(46.47, -7.5) * mm, "radius": 2.02 * mm});
            skSolve(sketch);
        }
        {
            var Q0;
            Q0 = qSketchRegion(id + "F51", true);
            extrude(context, id + "F52", {"entities" : qUnion([Q0]), "operationType" : NewBodyOperationType.ADD, "oppositeDirection" : true, "depth" : 2 * mm});
        }
        {
            var Q0;
            {var subQ0=sQuery(id+"F0.wireOp",EDGE,"E0.left");var subQ1=sQuery(id+"F0.wireOp",EDGE,"E0.bottom");Q0=makeQuery(id+"F48.opPattern","COPY",FACE,{"derivedFrom":makeQuery(id+"F30.boolean.opBoolean","SPLIT",FACE,{"disambiguationData":[TD([makeQuery(id+"F7.boolean.opBoolean","COPY",FACE,{"derivedFrom":makeQuery(id+"F7.opExtrude","SWEPT_FACE",FACE,{"disambiguationData":[OSD([sQuery(id+"F6.wireOp",EDGE,"E3")])]})})])],"derivedFrom":makeQuery(id+"F1.opExtrude","CAP_FACE",FACE,{"disambiguationData":[OSD([subQ1,sQuery(id+"F0.wireOp",EDGE,"E0.top"),subQ0,sQuery(id+"F0.wireOp",EDGE,"E0.right")])],"isStart":true})}),"instanceName":"1"});}
            var sketch = newSketch(context, id + "F53", { "sketchPlane" : qUnion([Q0])});
            skCircle(sketch, "E73", {"center": v(23.27, -12.5) * mm, "radius": 2 * mm});
            skSolve(sketch);
        }
        {
            var Q0;
            Q0 = qSketchRegion(id + "F53", true);
            extrude(context, id + "F54", {"entities" : qUnion([Q0]), "operationType" : NewBodyOperationType.ADD, "depth" : 2 * mm, "hasSecondDirection" : true, "secondDirectionOppositeDirection" : true, "secondDirectionDepth" : 6.6 * mm});
        }
        {
            var Q0;
            Q0=makeQuery(id+"F54.opExtrude","CAP_FACE",FACE,{"disambiguationData":[OSD([sQuery(id+"F53.wireOp",EDGE,"E73")])],"isStart":false});
            var sketch = newSketch(context, id + "F55", { "sketchPlane" : qUnion([Q0])});
            skCircle(sketch, "E74", {"center": v(23.27, -12.5) * mm, "radius": 2.15 * mm});
            skSolve(sketch);
        }
        {
            var Q0;
            Q0 = qSketchRegion(id + "F55", true);
            extrude(context, id + "F56", {"entities" : qUnion([Q0]), "operationType" : NewBodyOperationType.ADD, "oppositeDirection" : true, "depth" : 5 * mm});
        }
        {
            var Q0;
            Q0=makeQuery(id+"F56.boolean.opBoolean","MERGE",FACE,{"derivedFrom":[makeQuery(id+"F54.opExtrude","CAP_FACE",FACE,{"disambiguationData":[OSD([sQuery(id+"F53.wireOp",EDGE,"E73")])],"isStart":false}),makeQuery(id+"F56.opExtrude","CAP_FACE",FACE,{"disambiguationData":[OSD([sQuery(id+"F55.wireOp",EDGE,"E74")])],"isStart":true})]});
            var sketch = newSketch(context, id + "F57", { "sketchPlane" : qUnion([Q0])});
            skCircle(sketch, "E75", {"center": v(23.27, -12.5) * mm, "radius": 1 * mm});
            skSolve(sketch);
        }
        {
            var Q0;
            Q0 = qSketchRegion(id + "F57", true);
            extrude(context, id + "F58", {"entities" : qUnion([Q0]), "operationType" : NewBodyOperationType.REMOVE, "oppositeDirection" : true, "depth" : 5 * mm});
        }
        {
            var Q0;
            {var subQ0=sQuery(id+"F0.wireOp",EDGE,"E0.left");var subQ1=sQuery(id+"F0.wireOp",EDGE,"E0.top");var subQ2=sQuery(id+"F0.wireOp",EDGE,"E0.right");var subQ3=sQuery(id+"F0.wireOp",EDGE,"E0.bottom");Q0=makeQuery(id+"F48.opPattern","COPY",FACE,{"derivedFrom":makeQuery(id+"F30.boolean.opBoolean","SPLIT",FACE,{"disambiguationData":[TD([makeQuery(id+"F1.opExtrude","SWEPT_FACE",FACE,{"disambiguationData":[OSD([subQ1])]})])],"derivedFrom":makeQuery(id+"F1.opExtrude","CAP_FACE",FACE,{"disambiguationData":[OSD([subQ3,subQ1,subQ0,subQ2])],"isStart":true})}),"instanceName":"1"});}
            var sketch = newSketch(context, id + "F59", { "sketchPlane" : qUnion([Q0])});
            skCircle(sketch, "E76", {"center": v(37.47, -30.5) * mm, "radius": 2.1 * mm});
            skSolve(sketch);
        }
        {
            var Q0;
            Q0 = qSketchRegion(id + "F59", true);
            extrude(context, id + "F60", {"entities" : qUnion([Q0]), "operationType" : NewBodyOperationType.ADD, "depth" : 2 * mm, "hasSecondDirection" : true, "secondDirectionOppositeDirection" : true, "secondDirectionDepth" : 6.6 * mm});
        }
        {
            var Q0;
            Q0=makeQuery(id+"F60.opExtrude","CAP_FACE",FACE,{"disambiguationData":[OSD([sQuery(id+"F59.wireOp",EDGE,"E76")])],"isStart":false});
            var sketch = newSketch(context, id + "F61", { "sketchPlane" : qUnion([Q0])});
            skCircle(sketch, "E77", {"center": v(37.47, -30.5) * mm, "radius": 1 * mm});
            skSolve(sketch);
        }
        {
            var Q0;
            Q0 = qSketchRegion(id + "F61", true);
            extrude(context, id + "F62", {"entities" : qUnion([Q0]), "operationType" : NewBodyOperationType.REMOVE, "oppositeDirection" : true, "depth" : 5 * mm});
        }
        {
            var Q0;
            {var subQ0=sQuery(id+"F0.wireOp",EDGE,"E0.left");var subQ1=sQuery(id+"F0.wireOp",EDGE,"E0.bottom");Q0=makeQuery(id+"F48.opPattern","COPY",FACE,{"derivedFrom":makeQuery(id+"F30.boolean.opBoolean","SPLIT",FACE,{"disambiguationData":[TD([makeQuery(id+"F7.boolean.opBoolean","COPY",FACE,{"derivedFrom":makeQuery(id+"F7.opExtrude","SWEPT_FACE",FACE,{"disambiguationData":[OSD([sQuery(id+"F6.wireOp",EDGE,"E3")])]})})])],"derivedFrom":makeQuery(id+"F1.opExtrude","CAP_FACE",FACE,{"disambiguationData":[OSD([subQ1,sQuery(id+"F0.wireOp",EDGE,"E0.top"),subQ0,sQuery(id+"F0.wireOp",EDGE,"E0.right")])],"isStart":true})}),"instanceName":"1"});}
            var sketch = newSketch(context, id + "F63", { "sketchPlane" : qUnion([Q0])});
            skCircle(sketch, "E78", {"center": v(-41.33, -18.7) * mm, "radius": 2.1 * mm});
            skSolve(sketch);
        }
        {
            var Q0;
            Q0 = qSketchRegion(id + "F63", true);
            extrude(context, id + "F64", {"entities" : qUnion([Q0]), "operationType" : NewBodyOperationType.ADD, "depth" : 2 * mm, "hasSecondDirection" : true, "secondDirectionOppositeDirection" : true, "secondDirectionDepth" : 6.6 * mm});
        }
        {
            var Q0;
            Q0=makeQuery(id+"F64.opExtrude","CAP_FACE",FACE,{"disambiguationData":[OSD([sQuery(id+"F63.wireOp",EDGE,"E78")])],"isStart":false});
            var sketch = newSketch(context, id + "F65", { "sketchPlane" : qUnion([Q0])});
            skCircle(sketch, "E79", {"center": v(-41.33, -18.7) * mm, "radius": 1 * mm});
            skSolve(sketch);
        }
        {
            var Q0;
            Q0 = qSketchRegion(id + "F65", true);
            extrude(context, id + "F66", {"entities" : qUnion([Q0]), "operationType" : NewBodyOperationType.REMOVE, "oppositeDirection" : true, "depth" : 5 * mm});
        }
        {
            var Q0;
            Q0=makeQuery(id+"F48.opPattern","COPY",FACE,{"derivedFrom":makeQuery(id+"F47.boolean.opBoolean","COPY",FACE,{"derivedFrom":makeQuery(id+"F47.opExtrude","CAP_FACE",FACE,{"disambiguationData":[OSD([sQuery(id+"F46.wireOp",EDGE,"E69.bottom"),sQuery(id+"F46.wireOp",EDGE,"E69.top"),sQuery(id+"F46.wireOp",EDGE,"E69.left"),sQuery(id+"F46.wireOp",EDGE,"E69.right")])],"isStart":false})}),"instanceName":"1"});
            var sketch = newSketch(context, id + "F67", { "sketchPlane" : qUnion([Q0])});
            skLineSegment(sketch, "E80.bottom", {"start": v(-51.33, -22.3) * mm, "end": v(-55.53, -22.3) * mm});
            skLineSegment(sketch, "E80.top", {"start": v(-51.33, -25.5) * mm, "end": v(-55.53, -25.5) * mm});
            skLineSegment(sketch, "E80.left", {"start": v(-51.33, -22.3) * mm, "end": v(-51.33, -25.5) * mm});
            skLineSegment(sketch, "E80.right", {"start": v(-55.53, -22.3) * mm, "end": v(-55.53, -25.5) * mm});
            skSolve(sketch);
        }
        {
            var Q0;
            Q0 = qSketchRegion(id + "F67", true);
            var Q1;
            {var subQ0=sQuery(id+"F0.wireOp",EDGE,"E0.left");var subQ1=sQuery(id+"F0.wireOp",EDGE,"E0.bottom");Q1=makeQuery(id+"F48.opPattern","COPY",FACE,{"derivedFrom":makeQuery(id+"F30.boolean.opBoolean","SPLIT",FACE,{"disambiguationData":[TD([makeQuery(id+"F7.boolean.opBoolean","COPY",FACE,{"derivedFrom":makeQuery(id+"F7.opExtrude","SWEPT_FACE",FACE,{"disambiguationData":[OSD([sQuery(id+"F6.wireOp",EDGE,"E3")])]})})])],"derivedFrom":makeQuery(id+"F1.opExtrude","CAP_FACE",FACE,{"disambiguationData":[OSD([subQ1,sQuery(id+"F0.wireOp",EDGE,"E0.top"),subQ0,sQuery(id+"F0.wireOp",EDGE,"E0.right")])],"isStart":true})}),"instanceName":"1"});}
            var Q2;
            Q2=makeQuery(id+"F48.opPattern","COPY",BODY,{"derivedFrom":makeQuery(id+"F1.opExtrude","SWEPT_BODY",BODY,{"disambiguationData":[OSD([sQuery(id+"F0.wireOp",EDGE,"E0.bottom"),sQuery(id+"F0.wireOp",EDGE,"E0.top"),sQuery(id+"F0.wireOp",EDGE,"E0.left"),sQuery(id+"F0.wireOp",EDGE,"E0.right")])]}),"instanceName":"1"});
            extrude(context, id + "F68", {"entities" : qUnion([Q0]), "operationType" : NewBodyOperationType.ADD, "endBound" : BoundingType.UP_TO_SURFACE, "endBoundEntityFace" : qUnion([Q1]), "endBoundEntityBody" : qUnion([Q2]), "depth" : 25 * mm});
        }
        {
            var Q0;
            Q0=makeQuery(id+"F47.boolean.opBoolean","COPY",FACE,{"derivedFrom":makeQuery(id+"F47.opExtrude","CAP_FACE",FACE,{"disambiguationData":[OSD([sQuery(id+"F46.wireOp",EDGE,"E69.bottom"),sQuery(id+"F46.wireOp",EDGE,"E69.top"),sQuery(id+"F46.wireOp",EDGE,"E69.left"),sQuery(id+"F46.wireOp",EDGE,"E69.right")])],"isStart":false})});
            var sketch = newSketch(context, id + "F69", { "sketchPlane" : qUnion([Q0])});
            skLineSegment(sketch, "E81.bottom", {"start": v(51.33, -22.3) * mm, "end": v(55.53, -22.3) * mm});
            skLineSegment(sketch, "E81.top", {"start": v(51.33, -25.5) * mm, "end": v(55.53, -25.5) * mm});
            skLineSegment(sketch, "E81.left", {"start": v(51.33, -22.3) * mm, "end": v(51.33, -25.5) * mm});
            skLineSegment(sketch, "E81.right", {"start": v(55.53, -22.3) * mm, "end": v(55.53, -25.5) * mm});
            skSolve(sketch);
        }
        {
            var Q0;
            Q0 = qSketchRegion(id + "F69", true);
            var Q1;
            {var subQ0=sQuery(id+"F0.wireOp",EDGE,"E0.left");var subQ1=sQuery(id+"F0.wireOp",EDGE,"E0.bottom");Q1=makeQuery(id+"F30.boolean.opBoolean","SPLIT",FACE,{"disambiguationData":[TD([makeQuery(id+"F7.boolean.opBoolean","COPY",FACE,{"derivedFrom":makeQuery(id+"F7.opExtrude","SWEPT_FACE",FACE,{"disambiguationData":[OSD([sQuery(id+"F6.wireOp",EDGE,"E3")])]})})])],"derivedFrom":makeQuery(id+"F1.opExtrude","CAP_FACE",FACE,{"disambiguationData":[OSD([subQ1,sQuery(id+"F0.wireOp",EDGE,"E0.top"),subQ0,sQuery(id+"F0.wireOp",EDGE,"E0.right")])],"isStart":true})});}
            extrude(context, id + "F70", {"entities" : qUnion([Q0]), "operationType" : NewBodyOperationType.ADD, "endBound" : BoundingType.UP_TO_SURFACE, "endBoundEntityFace" : qUnion([Q1]), "depth" : 25 * mm});
        }
        {
            var Q0;
            {var subQ0=sQuery(id+"F0.wireOp",EDGE,"E0.left");var subQ1=sQuery(id+"F0.wireOp",EDGE,"E0.bottom");Q0=makeQuery(id+"F70.boolean.opBoolean","MERGE",FACE,{"derivedFrom":[makeQuery(id+"F30.boolean.opBoolean","SPLIT",FACE,{"disambiguationData":[TD([makeQuery(id+"F7.boolean.opBoolean","COPY",FACE,{"derivedFrom":makeQuery(id+"F7.opExtrude","SWEPT_FACE",FACE,{"disambiguationData":[OSD([sQuery(id+"F6.wireOp",EDGE,"E3")])]})})])],"derivedFrom":makeQuery(id+"F1.opExtrude","CAP_FACE",FACE,{"disambiguationData":[OSD([subQ1,sQuery(id+"F0.wireOp",EDGE,"E0.top"),subQ0,sQuery(id+"F0.wireOp",EDGE,"E0.right")])],"isStart":true})}),makeQuery(id+"F70.opExtrude","CAP_FACE",FACE,{"disambiguationData":[OSD([sQuery(id+"F69.wireOp",EDGE,"E81.bottom"),sQuery(id+"F69.wireOp",EDGE,"E81.top"),sQuery(id+"F69.wireOp",EDGE,"E81.left"),sQuery(id+"F69.wireOp",EDGE,"E81.right")])],"isStart":false})]});}
            var sketch = newSketch(context, id + "F71", { "sketchPlane" : qUnion([Q0])});
            skCircle(sketch, "E82", {"center": v(41.33, -18.7) * mm, "radius": 2.2 * mm});
            skCircle(sketch, "E83", {"center": v(-23.27, -12.5) * mm, "radius": 2.2 * mm});
            skSolve(sketch);
        }
        {
            var Q0;
            Q0 = qSketchRegion(id + "F71", true);
            extrude(context, id + "F72", {"entities" : qUnion([Q0]), "operationType" : NewBodyOperationType.REMOVE, "oppositeDirection" : true, "depth" : 2 * mm});
        }
        {
            var Q0;
            Q0=makeQuery(id+"F28.imprint","IMPRINT",FACE,{"disambiguationData":[TD([[makeQuery(id+"F28.imprint","IMPRINT",EDGE,{"derivedFrom":sQuery(id+"F28.wireOp",EDGE,"E14.top")}),1.0]])]});
            var sketch = newSketch(context, id + "F73", { "sketchPlane" : qUnion([Q0])});
            skCircle(sketch, "E84", {"center": v(23.27, -12.5) * mm, "radius": 2 * mm});
            skSolve(sketch);
        }
        {
            var Q0;
            Q0 = qSketchRegion(id + "F73", true);
            extrude(context, id + "F74", {"entities" : qUnion([Q0]), "operationType" : NewBodyOperationType.REMOVE, "oppositeDirection" : true, "depth" : 3.5 * mm});
        }
        {
            var Q0;
            {var subQ0=sQuery(id+"F0.wireOp",EDGE,"E0.left");var subQ1=sQuery(id+"F0.wireOp",EDGE,"E0.top");var subQ2=sQuery(id+"F0.wireOp",EDGE,"E0.right");var subQ3=sQuery(id+"F0.wireOp",EDGE,"E0.bottom");Q0=makeQuery(id+"F30.boolean.opBoolean","SPLIT",FACE,{"disambiguationData":[TD([makeQuery(id+"F1.opExtrude","SWEPT_FACE",FACE,{"disambiguationData":[OSD([subQ1])]})])],"derivedFrom":makeQuery(id+"F1.opExtrude","CAP_FACE",FACE,{"disambiguationData":[OSD([subQ3,subQ1,subQ0,subQ2])],"isStart":true})});}
            var sketch = newSketch(context, id + "F75", { "sketchPlane" : qUnion([Q0])});
            skCircle(sketch, "E85", {"center": v(-37.47, -30.5) * mm, "radius": 2.15 * mm});
            skSolve(sketch);
        }
        {
            var Q0;
            Q0 = qSketchRegion(id + "F75", true);
            extrude(context, id + "F76", {"entities" : qUnion([Q0]), "operationType" : NewBodyOperationType.REMOVE, "oppositeDirection" : true, "depth" : 3 * mm});
        }
        {
            var Q0;
            {var subQ0=sQuery(id+"F0.wireOp",EDGE,"E0.left");var subQ1=sQuery(id+"F0.wireOp",EDGE,"E0.top");var subQ2=sQuery(id+"F0.wireOp",EDGE,"E0.right");var subQ3=sQuery(id+"F0.wireOp",EDGE,"E0.bottom");Q0=makeQuery(id+"F30.boolean.opBoolean","SPLIT",FACE,{"disambiguationData":[TD([makeQuery(id+"F1.opExtrude","SWEPT_FACE",FACE,{"disambiguationData":[OSD([subQ1])]})])],"derivedFrom":makeQuery(id+"F1.opExtrude","CAP_FACE",FACE,{"disambiguationData":[OSD([subQ3,subQ1,subQ0,subQ2])],"isStart":true})});}
            var sketch = newSketch(context, id + "F77", { "sketchPlane" : qUnion([Q0])});
            skCircle(sketch, "E86", {"center": v(-46.47, -7.5) * mm, "radius": 2.1 * mm});
            skSolve(sketch);
        }
        {
            var Q0;
            Q0 = qSketchRegion(id + "F77", true);
            extrude(context, id + "F78", {"entities" : qUnion([Q0]), "operationType" : NewBodyOperationType.REMOVE, "oppositeDirection" : true, "depth" : 3 * mm});
        }
        {
            var Q0;
            Q0=makeQuery(id+"F50.opExtrude","CAP_FACE",FACE,{"disambiguationData":[OSD([sQuery(id+"F49.wireOp",EDGE,"E70")])],"isStart":false});
            var sketch = newSketch(context, id + "F79", { "sketchPlane" : qUnion([Q0])});
            skCircle(sketch, "E87", {"center": v(46.47, -7.5) * mm, "radius": 1 * mm});
            skSolve(sketch);
        }
        {
            var Q0;
            Q0 = qSketchRegion(id + "F79", true);
            extrude(context, id + "F80", {"entities" : qUnion([Q0]), "operationType" : NewBodyOperationType.REMOVE, "oppositeDirection" : true, "depth" : 5 * mm});
        }
    });
